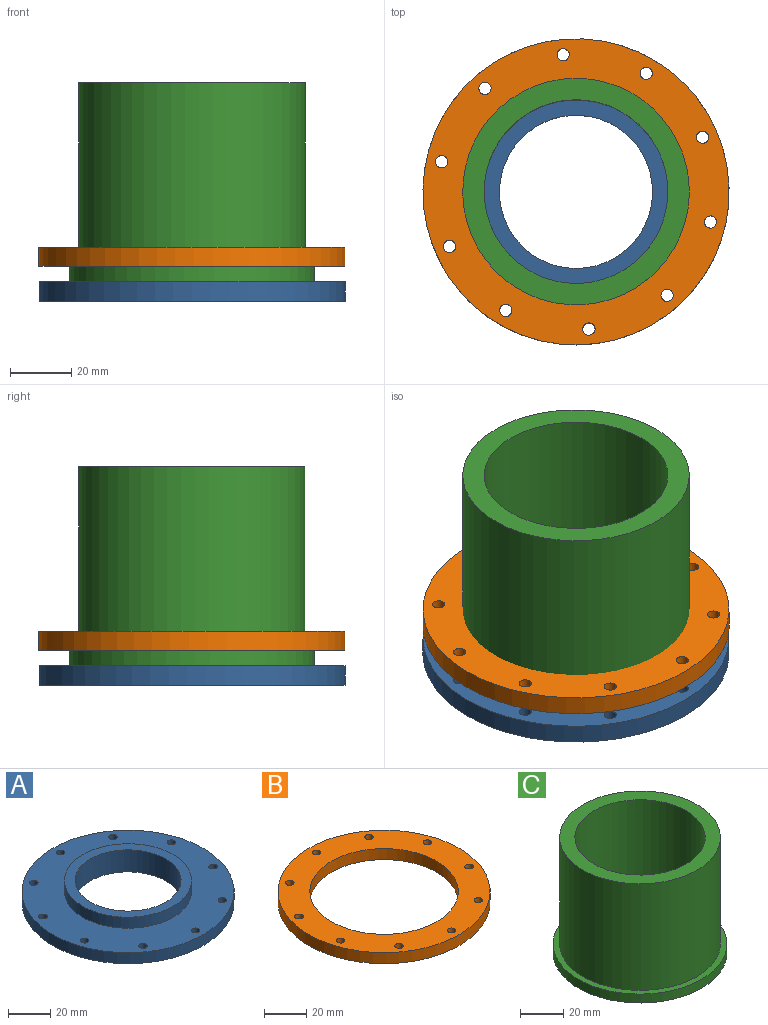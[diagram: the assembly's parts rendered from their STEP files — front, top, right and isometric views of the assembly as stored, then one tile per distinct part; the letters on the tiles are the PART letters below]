
ASSEMBLY  parts=3 mates=5
PART A: 16 faces, bbox 100x100x12.7 mm
  f0: cylinder r=25mm len=50mm, axis (0,0,-1), area 1994.9mm2, adj f3,f5
  f1: cylinder r=50mm len=100mm, axis (0,0,-1), area 1994.9mm2, adj f2,f3
  f2: plane 100x100mm, normal (0,0,1), area 4900.9mm2, adj f1,f4,f6,f7,f8,f9,f10,f11
  f3: plane 100x100mm, normal (0,0,-1), area 5764.8mm2, adj f0,f1,f6,f7,f8,f9,f10,f11
  f4: cylinder r=30mm len=60mm, axis (0,0,-1), area 1196.9mm2, adj f2,f5
  f5: plane 60x60mm, normal (0,0,1), area 863.9mm2, adj f0,f4
  f6: cylinder r=2mm len=6.35mm, axis (0,0,1), area 79.8mm2, adj f2,f3
  f7: cylinder r=2mm len=6.35mm, axis (0,0,1), area 79.8mm2, adj f2,f3
  f8: cylinder r=2mm len=6.35mm, axis (0,0,1), area 79.8mm2, adj f2,f3
  f9: cylinder r=2mm len=6.35mm, axis (0,0,1), area 79.8mm2, adj f2,f3
  f10: cylinder r=2mm len=6.35mm, axis (0,0,1), area 79.8mm2, adj f2,f3
  f11: cylinder r=2mm len=6.35mm, axis (0,0,1), area 79.8mm2, adj f2,f3
  f12: cylinder r=2mm len=6.35mm, axis (0,0,1), area 79.8mm2, adj f2,f3
  f13: cylinder r=2mm len=6.35mm, axis (0,0,1), area 79.8mm2, adj f2,f3
  f14: cylinder r=2mm len=6.35mm, axis (0,0,1), area 79.8mm2, adj f2,f3
  f15: cylinder r=2mm len=6.35mm, axis (0,0,1), area 79.8mm2, adj f2,f3
PART B: 14 faces, bbox 100x100x6.4 mm
  f0: cylinder r=50mm len=100mm, axis (0,0,-1), area 1994.9mm2, adj f1,f2
  f1: plane 100x100mm, normal (0,0,1), area 3879.9mm2, adj f0,f3,f4,f5,f6,f7,f8,f9
  f2: plane 100x100mm, normal (0,0,-1), area 3879.9mm2, adj f0,f3,f4,f5,f6,f7,f8,f9
  f3: cylinder r=2mm len=6.35mm, axis (0,0,1), area 79.8mm2, adj f1,f2
  f4: cylinder r=2mm len=6.35mm, axis (0,0,1), area 79.8mm2, adj f1,f2
  f5: cylinder r=2mm len=6.35mm, axis (0,0,1), area 79.8mm2, adj f1,f2
  f6: cylinder r=2mm len=6.35mm, axis (0,0,1), area 79.8mm2, adj f1,f2
  f7: cylinder r=2mm len=6.35mm, axis (0,0,1), area 79.8mm2, adj f1,f2
  f8: cylinder r=2mm len=6.35mm, axis (0,0,1), area 79.8mm2, adj f1,f2
  f9: cylinder r=2mm len=6.35mm, axis (0,0,1), area 79.8mm2, adj f1,f2
  f10: cylinder r=2mm len=6.35mm, axis (0,0,1), area 79.8mm2, adj f1,f2
  f11: cylinder r=35mm len=70mm, axis (0,0,1), area 1396.4mm2, adj f1,f2
  f12: cylinder r=2mm len=6.35mm, axis (0,0,1), area 79.8mm2, adj f1,f2
  f13: cylinder r=2mm len=6.35mm, axis (0,0,1), area 79.8mm2, adj f1,f2
PART C: 6 faces, bbox 80x80x65 mm
  f0: cylinder r=30mm len=65mm, axis (0,0,-1), area 12252.2mm2, adj f3,f5
  f1: cylinder r=40mm len=80mm, axis (0,0,-1), area 1256.6mm2, adj f2,f3
  f2: plane 80x80mm, normal (0,0,1), area 725.7mm2, adj f1,f4
  f3: plane 80x80mm, normal (0,0,-1), area 2199.1mm2, adj f0,f1
  f4: cylinder r=37mm len=74mm, axis (0,0,-1), area 13948.7mm2, adj f2,f5
  f5: plane 74x74mm, normal (0,0,1), area 1473.4mm2, adj f0,f4
PLACE A rot(axis=(0,0,-1),174.6deg) t=(0,0,-11.26)mm
PLACE B rot(axis=(0.35,-0.94,0),180deg) t=(0,0,6.44)mm
PLACE C rot(axis=(0,0,1),61.7deg) t=(0,0,-4.91)mm
MATE cylindrical B.f8 <-> A.f15  axis (0,0,1) through (4.21,-44.8,6.44)mm
MATE cylindrical A.f1 <-> B.f0  axis (0,0,1) through (0,0,-4.91)mm
MATE planar A.f1 <-> B.f11  axis (0,0,1) through (0,0,-4.91)mm
MATE cylindrical C.f1 <-> A.f0  axis (0,0,1) through (0,0,0.09)mm
MATE planar A.f1 <-> C.f0  axis (0,0,1) through (0,0,-4.91)mm
